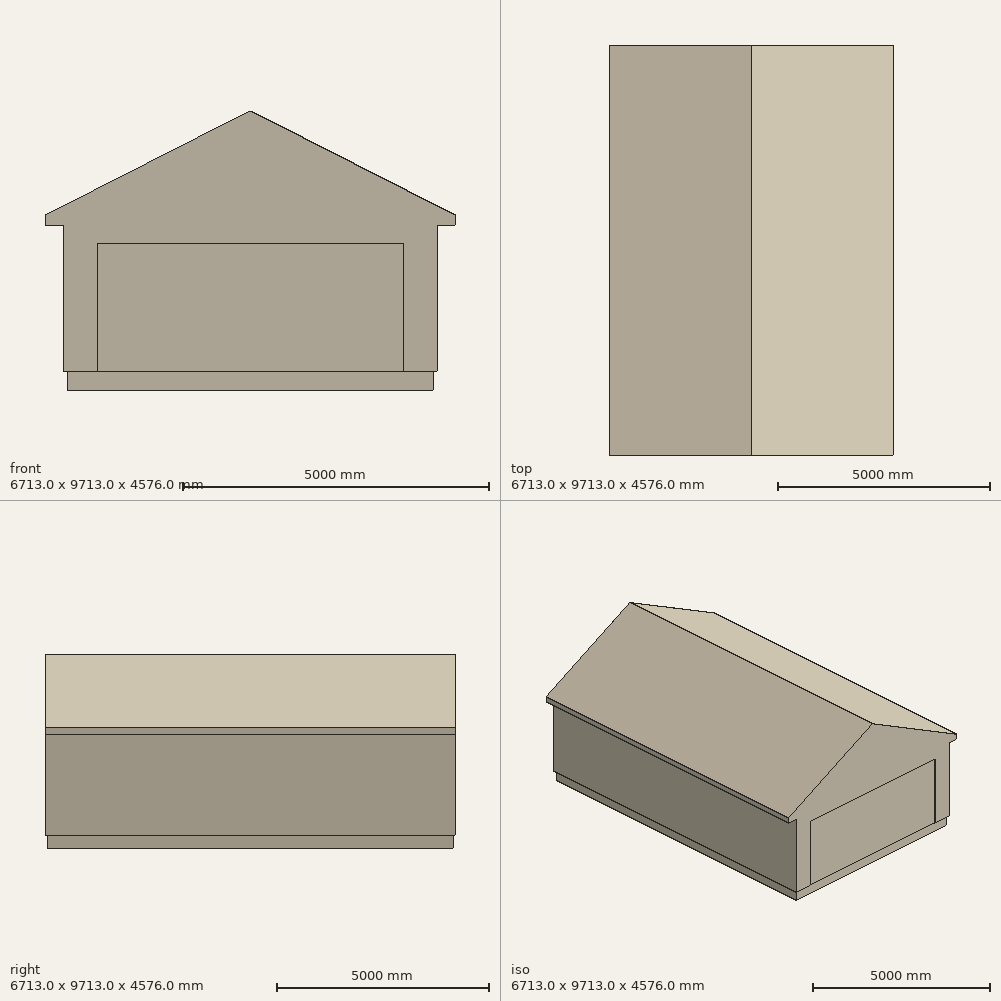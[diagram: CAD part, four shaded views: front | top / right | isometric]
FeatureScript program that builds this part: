
annotation { "Feature Type Name" : "Feature", "Feature Type Description" : "" }
export const myFeature = defineFeature(function(context is Context, id is Id, definition is map)
    precondition{}
    {
        {
            var Q0;
            Q0=qCreatedBy(makeId("Top.planeOp"),FACE);
            var sketch = newSketch(context, id + "F0", { "sketchPlane" : qUnion([Q0])});
            skLineSegment(sketch, "E0.bottom", {"start": v(0, 0) * mm, "end": v(6000, 0) * mm});
            skLineSegment(sketch, "E0.top", {"start": v(0, -9600) * mm, "end": v(6000, -9600) * mm});
            skLineSegment(sketch, "E0.left", {"start": v(0, 0) * mm, "end": v(0, -9600) * mm});
            skLineSegment(sketch, "E0.right", {"start": v(6000, 0) * mm, "end": v(6000, -9600) * mm});
            skSolve(sketch);
        }
        {
            var Q0;
            Q0=makeQuery(id+"F0.imprint","IMPRINT",FACE,{"disambiguationData":[TD([[makeQuery(id+"F0.imprint","IMPRINT",EDGE,{"derivedFrom":sQuery(id+"F0.wireOp",EDGE,"E0.bottom")}),-1.0]])]});
            extrude(context, id + "F1", {"entities" : qUnion([Q0]), "depth" : 300 * mm, "offsetDistance" : 25 * mm});
        }
        {
            var Q0;
            Q0=makeQuery(id+"F1.opExtrude","CAP_FACE",FACE,{"disambiguationData":[OSD([sQuery(id+"F0.wireOp",EDGE,"E0.bottom"),sQuery(id+"F0.wireOp",EDGE,"E0.top"),sQuery(id+"F0.wireOp",EDGE,"E0.left"),sQuery(id+"F0.wireOp",EDGE,"E0.right")])],"isStart":false});
            var sketch = newSketch(context, id + "F2", { "sketchPlane" : qUnion([Q0])});
            skLineSegment(sketch, "E1.bottom", {"start": v(-56.5, 56.5) * mm, "end": v(6056.5, 56.5) * mm});
            skLineSegment(sketch, "E1.top", {"start": v(-56.5, -9656.5) * mm, "end": v(6056.5, -9656.5) * mm});
            skLineSegment(sketch, "E1.left", {"start": v(-56.5, 56.5) * mm, "end": v(-56.5, -9656.5) * mm});
            skLineSegment(sketch, "E1.right", {"start": v(6056.5, 56.5) * mm, "end": v(6056.5, -9656.5) * mm});
            skLineSegment(sketch, "E2.0", {"start": v(143.5, -143.5) * mm, "end": v(5856.5, -143.5) * mm});
            skLineSegment(sketch, "E2.1", {"start": v(143.5, -143.5) * mm, "end": v(143.5, -9456.5) * mm});
            skLineSegment(sketch, "E2.2", {"start": v(143.5, -9456.5) * mm, "end": v(5856.5, -9456.5) * mm});
            skLineSegment(sketch, "E2.3", {"start": v(5856.5, -143.5) * mm, "end": v(5856.5, -9456.5) * mm});
            skSolve(sketch);
        }
        {
            var Q0;
            Q0 = qSketchRegion(id + "F2", true);
            extrude(context, id + "F3", {"entities" : qUnion([Q0]), "depth" : 2400 * mm, "offsetDistance" : 25 * mm});
        }
        {
            var Q0;
            Q0=makeQuery(id+"F3.opExtrude","SWEPT_FACE",FACE,{"disambiguationData":[OSD([sQuery(id+"F2.wireOp",EDGE,"E1.top")])]});
            var sketch = newSketch(context, id + "F4", { "sketchPlane" : qUnion([Q0])});
            skLineSegment(sketch, "E3", {"start": v(3000, 4576) * mm, "end": v(-356.5, 2865.78) * mm});
            skPoint(sketch, "E3.startSnap0", {"position": v(3000, 2700) * mm});
            skPoint(sketch, "E3.endSnap0", {"position": v(3000, 2700) * mm});
            skLineSegment(sketch, "E4", {"start": v(-356.5, 2700) * mm, "end": v(6356.5, 2700) * mm});
            skLineSegment(sketch, "E5", {"start": v(6356.5, 2865.78) * mm, "end": v(3000, 4576) * mm});
            skLineSegment(sketch, "E6", {"start": v(3000, 4576) * mm, "end": v(3000, 2700) * mm, "construction": true});
            skLineSegment(sketch, "E7", {"start": v(-356.5, 2865.78) * mm, "end": v(-356.5, 2700) * mm});
            skLineSegment(sketch, "E8", {"start": v(6356.5, 2865.78) * mm, "end": v(6356.5, 2700) * mm});
            skLineSegment(sketch, "E9", {"start": v(3000, 2700) * mm, "end": v(3000, 300) * mm, "construction": true});
            skPoint(sketch, "E10.orphan", {"position": v(-681.86, 2700) * mm});
            skSolve(sketch);
        }
        {
            var Q0;
            Q0 = qSketchRegion(id + "F4", true);
            var Q1;
            Q1=makeQuery(id+"F3.opExtrude","SWEPT_FACE",FACE,{"disambiguationData":[OSD([sQuery(id+"F2.wireOp",EDGE,"E1.bottom")])]});
            extrude(context, id + "F5", {"entities" : qUnion([Q0]), "operationType" : NewBodyOperationType.ADD, "endBound" : BoundingType.UP_TO_SURFACE, "oppositeDirection" : true, "depth" : 25 * mm, "endBoundEntityFace" : qUnion([Q1]), "offsetDistance" : 25 * mm});
        }
        {
            var Q0;
            Q0=makeQuery(id+"F5.boolean.opBoolean","MERGE",FACE,{"derivedFrom":[makeQuery(id+"F3.opExtrude","SWEPT_FACE",FACE,{"disambiguationData":[OSD([sQuery(id+"F2.wireOp",EDGE,"E1.top")])]}),makeQuery(id+"F5.opExtrude","CAP_FACE",FACE,{"disambiguationData":[OSD([sQuery(id+"F4.wireOp",EDGE,"E3"),sQuery(id+"F4.wireOp",EDGE,"E4"),sQuery(id+"F4.wireOp",EDGE,"E5"),sQuery(id+"F4.wireOp",EDGE,"E7"),sQuery(id+"F4.wireOp",EDGE,"E8")])],"isStart":true})]});
            var sketch = newSketch(context, id + "F6", { "sketchPlane" : qUnion([Q0])});
            skLineSegment(sketch, "E11.bottom", {"start": v(500, 300) * mm, "end": v(5500, 300) * mm});
            skLineSegment(sketch, "E11.top", {"start": v(500, 2400) * mm, "end": v(5500, 2400) * mm});
            skLineSegment(sketch, "E11.left", {"start": v(500, 300) * mm, "end": v(500, 2400) * mm});
            skLineSegment(sketch, "E11.right", {"start": v(5500, 300) * mm, "end": v(5500, 2400) * mm});
            skPoint(sketch, "E12", {"position": v(3000, 300) * mm});
            skSolve(sketch);
        }
        {
            var Q0;
            Q0 = qSketchRegion(id + "F6", true);
            extrude(context, id + "F7", {"entities" : qUnion([Q0]), "operationType" : NewBodyOperationType.REMOVE, "endBound" : BoundingType.UP_TO_NEXT, "oppositeDirection" : true, "depth" : 25 * mm, "offsetDistance" : 25 * mm});
        }
        {
            var Q0;
            Q0=makeQuery(id+"F5.boolean.opBoolean","MERGE",FACE,{"derivedFrom":[makeQuery(id+"F3.opExtrude","SWEPT_FACE",FACE,{"disambiguationData":[OSD([sQuery(id+"F2.wireOp",EDGE,"E1.top")])]}),makeQuery(id+"F5.opExtrude","CAP_FACE",FACE,{"disambiguationData":[OSD([sQuery(id+"F4.wireOp",EDGE,"E3"),sQuery(id+"F4.wireOp",EDGE,"E4"),sQuery(id+"F4.wireOp",EDGE,"E5"),sQuery(id+"F4.wireOp",EDGE,"E7"),sQuery(id+"F4.wireOp",EDGE,"E8")])],"isStart":true})]});
            var sketch = newSketch(context, id + "F8", { "sketchPlane" : qUnion([Q0])});
            skLineSegment(sketch, "E13.bottom", {"start": v(500, 300) * mm, "end": v(5500, 300) * mm});
            skLineSegment(sketch, "E13.top", {"start": v(500, 2400) * mm, "end": v(5500, 2400) * mm});
            skLineSegment(sketch, "E13.left", {"start": v(500, 300) * mm, "end": v(500, 2400) * mm});
            skLineSegment(sketch, "E13.right", {"start": v(5500, 300) * mm, "end": v(5500, 2400) * mm});
            skSolve(sketch);
        }
        {
            var Q0;
            Q0 = qSketchRegion(id + "F8", true);
            extrude(context, id + "F9", {"entities" : qUnion([Q0]), "oppositeDirection" : true, "depth" : 100 * mm, "offsetDistance" : 25 * mm});
        }
        {
            var Q0;
            Q0=makeQuery(id+"F9.opExtrude","SWEPT_BODY",BODY,{"disambiguationData":[OSD([sQuery(id+"F8.wireOp",EDGE,"E13.bottom"),sQuery(id+"F8.wireOp",EDGE,"E13.top"),sQuery(id+"F8.wireOp",EDGE,"E13.left"),sQuery(id+"F8.wireOp",EDGE,"E13.right")])]});
            var Q1;
            Q1=makeQuery(id+"F3.opExtrude","CAP_EDGE",EDGE,{"disambiguationData":[OSD([sQuery(id+"F2.wireOp",EDGE,"E1.right")])],"isStart":true});
            transform(context, id + "F10", {"entities" : qUnion([Q0]), "transformType" : TransformType.TRANSLATION_3D, "dx" : 0 * mm, "dy" : 30 * mm, "dz" : 0 * mm, "makeCopy" : false});
        }
    });
